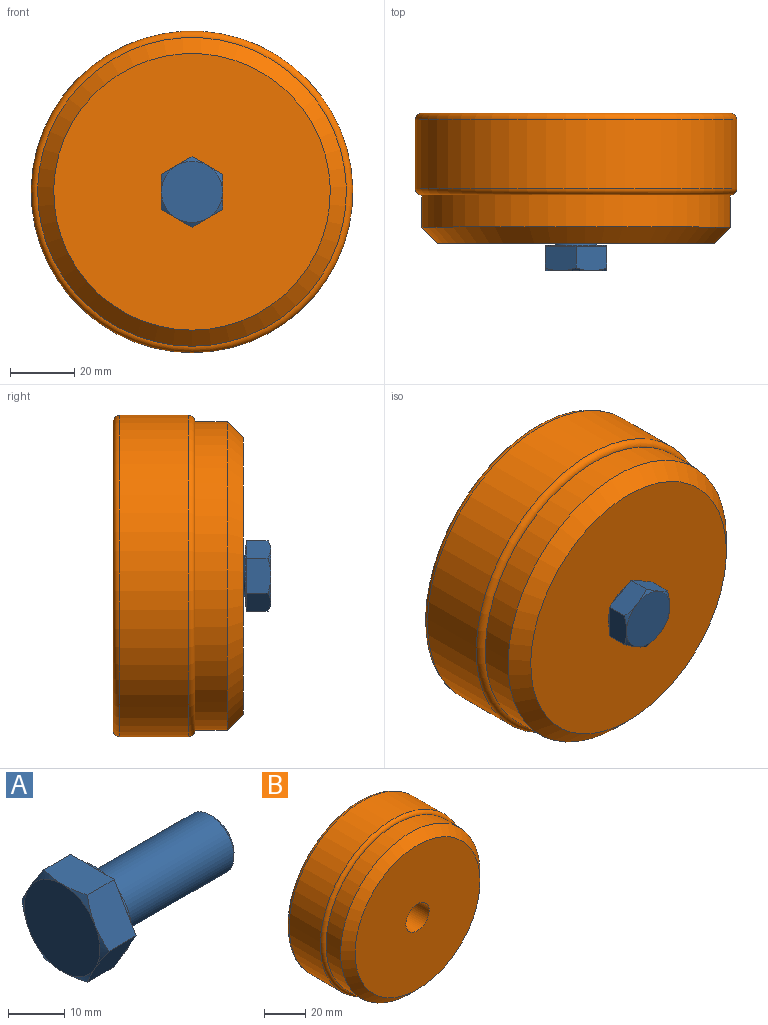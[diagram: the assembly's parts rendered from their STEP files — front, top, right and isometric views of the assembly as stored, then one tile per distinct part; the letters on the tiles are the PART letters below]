
ASSEMBLY  parts=2 mates=1
PART A: 25 faces, bbox 38x21.9x21.9 mm
  f0: plane 8.23x4.75mm, normal (1,0,0), area 4.9mm2, adj f6,f14,f15
  f1: plane 9.5x2.74mm, normal (1,0,0), area 4.9mm2, adj f6,f13,f14
  f2: plane 8.23x4.75mm, normal (1,0,0), area 4.9mm2, adj f6,f12,f13
  f3: plane 8.23x4.75mm, normal (1,0,0), area 4.9mm2, adj f6,f15,f16
  f4: plane 8.23x4.75mm, normal (1,0,0), area 4.9mm2, adj f6,f12,f17
  f5: plane 9.5x2.74mm, normal (1,0,0), area 4.9mm2, adj f6,f16,f17
  f6: cylinder r=9.5mm len=19mm, axis (1,0,0), area 23.9mm2, adj f0,f1,f2,f3,f4,f5,f7
  f7: plane 19x19mm, normal (1,0,0), area 146.7mm2, adj f6,f8
  f8: torus R=6.6mm, axis (1,0,0), area 36.8mm2, adj f7,f9
  f9: cylinder r=6mm len=28.63mm, axis (1,0,0), area 1079.4mm2, adj f8,f10
  f10: cone r=6mm half-angle=45deg, axis (-1,0,0), area 38.3mm2, adj f9,f11
  f11: plane 10.47x10.47mm, normal (1,0,0), area 86mm2, adj f10
  f12: plane 10.98x7.6mm, normal (0,0,1), area 80.2mm2, adj f2,f4,f13,f17,f18,f24
  f13: plane 9.5x7.6mm, normal (0,0.87,0.5), area 80.2mm2, adj f1,f2,f12,f14,f18,f22
  f14: plane 9.5x7.6mm, normal (0,0.87,-0.5), area 80.2mm2, adj f0,f1,f13,f15,f21,f22
  f15: plane 10.98x7.6mm, normal (0,0,-1), area 80.2mm2, adj f0,f3,f14,f16,f20,f21
  f16: plane 9.5x7.6mm, normal (0,-0.87,-0.5), area 80.2mm2, adj f3,f5,f15,f17,f19,f20
  f17: plane 9.5x7.6mm, normal (0,-0.87,0.5), area 80.2mm2, adj f4,f5,f12,f16,f19,f24
  f18: cone r=9.5mm half-angle=60deg, axis (1,0,0), area 5.6mm2, adj f12,f13,f23
  f19: cone r=9.5mm half-angle=60deg, axis (1,0,0), area 5.6mm2, adj f16,f17,f23
  f20: cone r=9.5mm half-angle=60deg, axis (1,0,0), area 5.6mm2, adj f15,f16,f23
  f21: cone r=9.5mm half-angle=60deg, axis (1,0,0), area 5.6mm2, adj f14,f15,f23
  f22: cone r=9.5mm half-angle=60deg, axis (1,0,0), area 5.6mm2, adj f13,f14,f23
  f23: plane 19x19mm, normal (-1,0,0), area 283.5mm2, adj f18,f19,f20,f21,f22,f24
  f24: cone r=9.5mm half-angle=60deg, axis (1,0,0), area 5.6mm2, adj f12,f17,f23
PART B: 11 faces, bbox 108.2x40.4x108.2 mm
  f0: cylinder r=6mm len=21.4mm, axis (0,1,0), area 806.8mm2, adj f3,f5
  f1: cylinder r=50mm len=100mm, axis (0,1,0), area 6723mm2, adj f4,f6
  f2: plane 96x96mm, normal (0,1,0), area 7037.2mm2, adj f3,f4
  f3: torus R=8mm, axis (0,-1,0), area 132.8mm2, adj f0,f2
  f4: torus R=48mm, axis (0,-1,0), area 972.6mm2, adj f1,f2
  f5: torus R=8mm, axis (0,-1,0), area 132.8mm2, adj f0,f8
  f6: torus R=48mm, axis (0,-1,0), area 972.6mm2, adj f1,f7
  f7: cylinder r=48mm len=96mm, axis (0,1,0), area 3015.9mm2, adj f6,f10
  f8: cylinder r=8mm len=16mm, axis (0,1,0), area 754mm2, adj f5,f9
  f9: plane 86x86mm, normal (0,-1,0), area 5607.7mm2, adj f8,f10
  f10: cone r=43mm half-angle=45deg, axis (0,1,0), area 2021.5mm2, adj f7,f9
PLACE A rot(axis=(0.58,0.58,0.58),120deg) t=(33.75,-0.48,23.95)mm
PLACE B t=(33.75,40.52,23.95)mm fixed
MATE fastened A.f6 <-> B.f0  axis (0,1,0) through (33.75,0.12,23.95)mm
